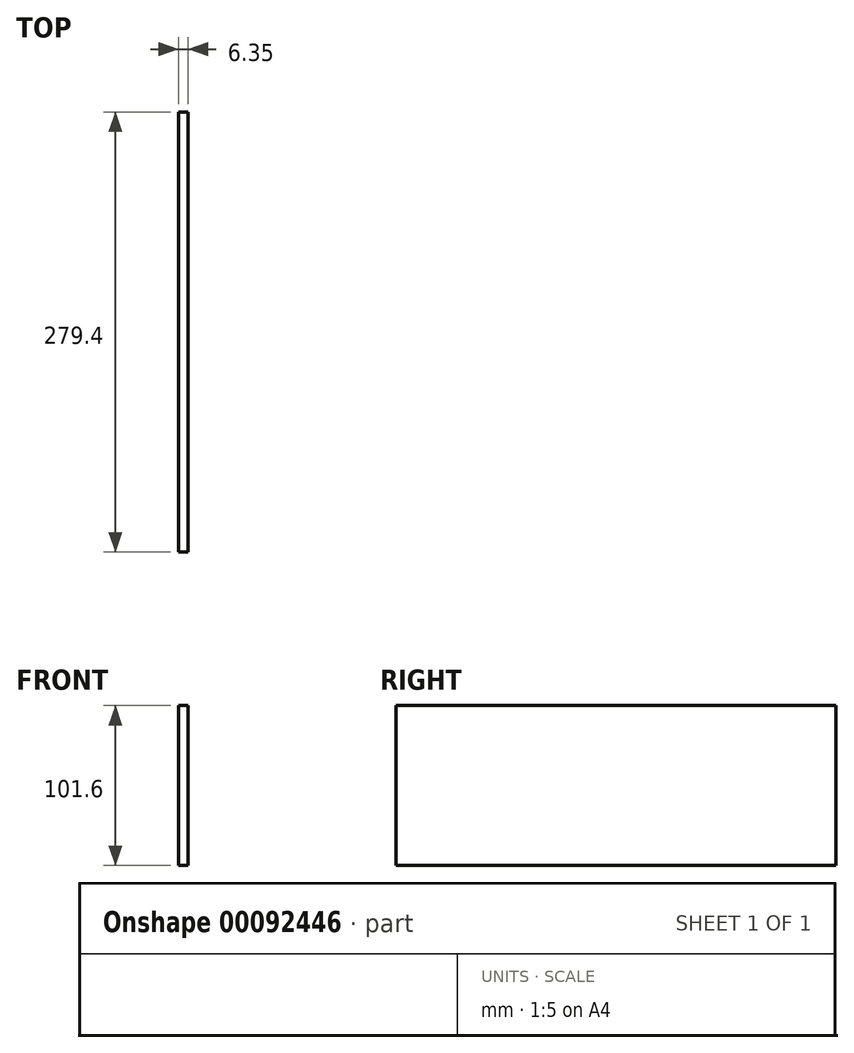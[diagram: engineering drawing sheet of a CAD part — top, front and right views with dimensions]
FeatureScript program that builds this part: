
annotation { "Feature Type Name" : "Feature", "Feature Type Description" : "" }
export const myFeature = defineFeature(function(context is Context, id is Id, definition is map)
    precondition{}
    {
        {
            var Q0;
            Q0=qCreatedBy(makeId("Front.planeOp"),FACE);
            var sketch = newSketch(context, id + "F0", { "sketchPlane" : qUnion([Q0])});
            skLineSegment(sketch, "E0.bottom", {"start": v(0, 0) * mm, "end": v(6.35, 0) * mm});
            skLineSegment(sketch, "E0.top", {"start": v(0, 101.6) * mm, "end": v(6.35, 101.6) * mm});
            skLineSegment(sketch, "E0.left", {"start": v(0, 0) * mm, "end": v(0, 101.6) * mm});
            skLineSegment(sketch, "E0.right", {"start": v(6.35, 0) * mm, "end": v(6.35, 101.6) * mm});
            skSolve(sketch);
        }
        {
            var Q0;
            Q0=makeQuery(id+"F0.imprint","IMPRINT",FACE,{"disambiguationData":[TD([[makeQuery(id+"F0.imprint","IMPRINT",EDGE,{"derivedFrom":sQuery(id+"F0.wireOp",EDGE,"E0.bottom")}),1.0]])]});
            extrude(context, id + "F1", {"entities" : qUnion([Q0]), "depth" : 279.4 * mm});
        }
    });
